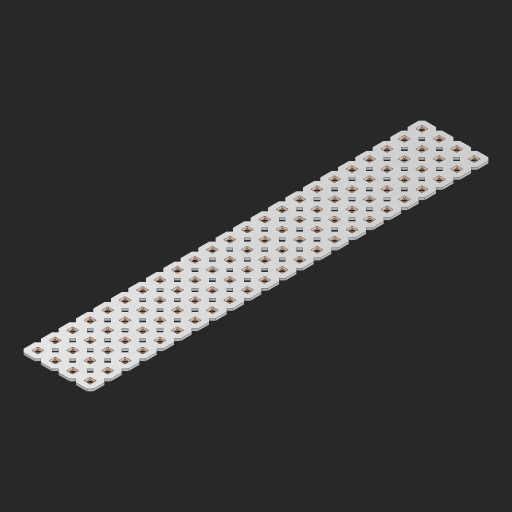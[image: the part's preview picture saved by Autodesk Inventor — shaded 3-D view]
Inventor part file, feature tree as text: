
AUTODESK INVENTOR PART (.ipt)
format: ipt  version: 2023 (Build 270158000, 158)  size: 1,341,440 bytes
history: native  units: in
note: dims shown in document units (in); Inventor stores cm internally (conversion verified against a paired STEP export)
features: other x93, extrude x91, sketch x2, pattern_linear x1
ambient origin geometry x8: Origin, YZ Plane, XZ Plane, XY Plane, X Axis, Y Axis, Z Axis, Center Point
bodies: Solid1 (feature_tree), Body (feature_tree)
feature tree (187):
  pattern_linear  "Rectangular Pattern1"  Spacing1=0.09in  [1 undecoded]
  sketch  "Sketch1"  dims[d1=0.5in]
  sketch  "Sketch2"  dims[d2=0.182in d3=0.09in d4=0.09in d5=0.09in d6=0.09in d7=0.09in d8=0.09in d9=0.09in d10=0.09in d11=0.02in d13=0.0in d14=0.172in d15=0.0625in d16=0.0in d19=0.5in d22=0.5in]
  other  "Srf1"
  other  "Srf126"
  other  "Srf127"
  other  "Srf128"
  other  "Srf129"
  other  "Srf130"
  other  "Srf131"
  other  "Srf250"
  other  "Srf251"
  other  "Srf252"
  other  "Srf253"
  other  "Srf254"
  other  "Srf255"
  other  "Srf256"
  other  "Srf257"
  other  "Srf258"
  other  "Srf259"
  other  "Srf260"
  other  "Srf261"
  other  "Srf262"
  other  "Srf263"
  other  "Srf264"
  other  "Srf265"
  other  "Srf268"
  other  "Srf269"
  other  "Srf270"
  other  "Srf271"
  other  "Srf272"
  other  "Srf273"
  other  "Srf274"
  other  "Srf275"
  other  "Srf276"
  other  "Srf277"
  other  "Srf278"
  other  "Srf279"
  other  "Srf280"
  other  "Srf281"
  other  "Srf282"
  other  "Srf283"
  other  "Srf284"
  other  "Srf285"
  other  "Srf286"
  other  "Srf287"
  other  "Srf288"
  other  "Srf289"
  other  "Srf290"
  other  "Srf293"
  other  "Srf294"
  other  "Srf295"
  other  "Srf296"
  other  "Srf297"
  other  "Srf298"
  other  "Srf299"
  other  "Srf300"
  other  "Srf301"
  other  "Srf302"
  other  "Srf303"
  other  "Srf304"
  other  "Srf305"
  other  "Srf306"
  other  "Srf307"
  other  "Srf308"
  other  "Srf309"
  other  "Srf310"
  other  "Srf311"
  other  "Srf312"
  other  "Srf313"
  other  "Srf314"
  other  "Srf315"
  other  "Srf318"
  other  "Srf319"
  other  "Srf320"
  other  "Srf321"
  other  "Srf322"
  other  "Srf323"
  other  "Srf324"
  other  "Srf325"
  other  "Srf326"
  other  "Srf327"
  other  "Srf328"
  other  "Srf329"
  other  "Srf330"
  other  "Srf331"
  other  "Srf332"
  other  "Srf333"
  other  "Srf334"
  other  "Srf335"
  other  "Srf336"
  other  "Srf337"
  other  "Srf338"
  other  "Srf339"
  other  "Srf340"
  other  "Circle"
  extrude  "ExtrusionSrf126"  Depth=0.09in
  extrude  "ExtrusionSrf127"  Depth=0.09in
  extrude  "ExtrusionSrf128"  Depth=0.09in
  extrude  "ExtrusionSrf129"  Depth=0.09in
  extrude  "ExtrusionSrf130"  Depth=0.09in
  extrude  "ExtrusionSrf131"  Depth=0.09in
  extrude  "ExtrusionSrf250"  Depth=0.09in
  extrude  "ExtrusionSrf251"  Depth=0.02in
  extrude  "ExtrusionSrf252"  TaperAngle=0.0deg  [1 undecoded]
  extrude  "ExtrusionSrf253"  Depth=0.5in
  extrude  "ExtrusionSrf254"  Depth=0.0625in TaperAngle=0.0deg
  extrude  "ExtrusionSrf255"  Depth=0.5in
  extrude  "ExtrusionSrf256"  Depth=0.5in
  extrude  "ExtrusionSrf257"  [1 undecoded]
  extrude  "ExtrusionSrf258"  [1 undecoded]
  extrude  "ExtrusionSrf259"  [1 undecoded]
  extrude  "ExtrusionSrf260"  [1 undecoded]
  extrude  "ExtrusionSrf261"  [1 undecoded]
  extrude  "ExtrusionSrf262"  [1 undecoded]
  extrude  "ExtrusionSrf263"  [1 undecoded]
  extrude  "ExtrusionSrf264"  [1 undecoded]
  extrude  "ExtrusionSrf265"  [1 undecoded]
  extrude  "ExtrusionSrf268"  [1 undecoded]
  extrude  "ExtrusionSrf269"  [1 undecoded]
  extrude  "ExtrusionSrf270"  [1 undecoded]
  extrude  "ExtrusionSrf271"  [1 undecoded]
  extrude  "ExtrusionSrf272"  [1 undecoded]
  extrude  "ExtrusionSrf273"  [1 undecoded]
  extrude  "ExtrusionSrf274"  [1 undecoded]
  extrude  "ExtrusionSrf275"  [1 undecoded]
  extrude  "ExtrusionSrf276"  [1 undecoded]
  extrude  "ExtrusionSrf277"  [1 undecoded]
  extrude  "ExtrusionSrf278"  [1 undecoded]
  extrude  "ExtrusionSrf279"  [1 undecoded]
  extrude  "ExtrusionSrf280"  [1 undecoded]
  extrude  "ExtrusionSrf281"  [1 undecoded]
  extrude  "ExtrusionSrf282"  [1 undecoded]
  extrude  "ExtrusionSrf283"  [1 undecoded]
  extrude  "ExtrusionSrf284"  [1 undecoded]
  extrude  "ExtrusionSrf285"  [1 undecoded]
  extrude  "ExtrusionSrf286"  [1 undecoded]
  extrude  "ExtrusionSrf287"  [1 undecoded]
  extrude  "ExtrusionSrf288"  [1 undecoded]
  extrude  "ExtrusionSrf289"  [1 undecoded]
  extrude  "ExtrusionSrf290"  [1 undecoded]
  extrude  "ExtrusionSrf293"  [1 undecoded]
  extrude  "ExtrusionSrf294"  [1 undecoded]
  extrude  "ExtrusionSrf295"  [1 undecoded]
  extrude  "ExtrusionSrf296"  [1 undecoded]
  extrude  "ExtrusionSrf297"  [1 undecoded]
  extrude  "ExtrusionSrf298"  [1 undecoded]
  extrude  "ExtrusionSrf299"  [1 undecoded]
  extrude  "ExtrusionSrf300"  [1 undecoded]
  extrude  "ExtrusionSrf301"  [1 undecoded]
  extrude  "ExtrusionSrf302"  [1 undecoded]
  extrude  "ExtrusionSrf303"  [1 undecoded]
  extrude  "ExtrusionSrf304"  [1 undecoded]
  extrude  "ExtrusionSrf305"  [1 undecoded]
  extrude  "ExtrusionSrf306"  [1 undecoded]
  extrude  "ExtrusionSrf307"  [1 undecoded]
  extrude  "ExtrusionSrf308"  [1 undecoded]
  extrude  "ExtrusionSrf309"  [1 undecoded]
  extrude  "ExtrusionSrf310"  [1 undecoded]
  extrude  "ExtrusionSrf311"  [1 undecoded]
  extrude  "ExtrusionSrf312"  [1 undecoded]
  extrude  "ExtrusionSrf313"  [1 undecoded]
  extrude  "ExtrusionSrf314"  [1 undecoded]
  extrude  "ExtrusionSrf315"  [1 undecoded]
  extrude  "ExtrusionSrf318"  [1 undecoded]
  extrude  "ExtrusionSrf319"  [1 undecoded]
  extrude  "ExtrusionSrf320"  [1 undecoded]
  extrude  "ExtrusionSrf321"  [1 undecoded]
  extrude  "ExtrusionSrf322"  [1 undecoded]
  extrude  "ExtrusionSrf323"  [1 undecoded]
  extrude  "ExtrusionSrf324"  [1 undecoded]
  extrude  "ExtrusionSrf325"  [1 undecoded]
  extrude  "ExtrusionSrf326"  [1 undecoded]
  extrude  "ExtrusionSrf327"  [1 undecoded]
  extrude  "ExtrusionSrf328"  [1 undecoded]
  extrude  "ExtrusionSrf329"  [1 undecoded]
  extrude  "ExtrusionSrf330"  [1 undecoded]
  extrude  "ExtrusionSrf331"  [1 undecoded]
  extrude  "ExtrusionSrf332"  [1 undecoded]
  extrude  "ExtrusionSrf333"  [1 undecoded]
  extrude  "ExtrusionSrf334"  [1 undecoded]
  extrude  "ExtrusionSrf335"  [1 undecoded]
  extrude  "ExtrusionSrf336"  [1 undecoded]
  extrude  "ExtrusionSrf337"  [1 undecoded]
  extrude  "ExtrusionSrf338"  [1 undecoded]
  extrude  "ExtrusionSrf339"  [1 undecoded]
  extrude  "ExtrusionSrf340"  [1 undecoded]
note: 80 required parameter values undecoded (feature->parameter linkage not recoverable at this tier; creation-order binding heuristic only, values carry confidence <= 0.55)
